# Revit family: Ventüer_VentilationLouvres_VL-77EX
name_source: partatom
category: Generic Models
units: mm (PartAtom-declared; Revit-internal decimal feet)

## family parameters
Always vertical = No
Can host rebar = No
Cut with Voids When Loaded = Yes
Part Type = Normal
Room Calculation Point = No
Round Connector Dimension = Use Diameter
Shared = No
Work Plane-Based = Yes

## types (3) — shared parameters
Aerodynamic Performance = Air Inlet: 0.244, Class 3. Air Extract: 0.255, Class 3
Ancillaries = Bird Mesh, Insect Mesh, Solid Blanking, Electric Actuators, Manual Lever Handles, Perimeter Mounting Angle
Blade Centres = 77 mm  [stored 0.252625 ft]
Blade Material = Ventüer Aluminium
Default Elevation = 1219 mm
Description = Maximum Airflow for Exhaust
Exact Neck Height = 594 mm  [stored 1.94882 ft]
Exact Neck Height Check = 594 mm  [stored 1.94882 ft]
Exact Neck Width = 594 mm  [stored 1.94882 ft]
Exact Neck Width Check = 594 mm  [stored 1.94882 ft]
Frame Material = Ventüer Aluminium
Frame Set Count = 1
Frame Set Count Check = 2
Frame Set Transition Count = 1
Frame Set Transition Count Check = 2
Manufacturer = Ventüer
Max Flow = 5000.0 L/s
Min Flow = 100.0 L/s
Model = VL-77EX
Multiple Frame Set = No
Multiple Transition = No
Noise Level NC Max = 0.00 NC
Noise Level NC Min = 0.00 NC
Nominal Height = 600 mm
Nominal Width = 600 mm
Nominated Air Flow = 100.0 L/s
Nominated Pessure Drop = 21.0 Pa
Rain Defence Performance = Class B - up to 0.5m/s suction velocity. Class C - up to 1.5m/s suction velocity. Class D - up to 3.5m/s suction velocity
SHS = No
Single Frame Set = Yes
Single Transition = No
Specified Air Flow = 0.0 L/s
Specified Pressure Drop = 21.0 Pa
Static Pressure Max = 60.0 Pa
Static Pressure Min = 10.0 Pa
Tee = Yes
URL = https://www.ventuer.co
Ventüer Product Range = Ventilation Louvres

## per-type parameters (varying)
| type | Base Width | Blade And Frame Gap | Blade Count | Blade Cut Offset | Blade Horizontal Offset | Channel | Connector Height | Connector Width | Depth | Flanged | Frame Set Width | Glazed | Keynote | Overall Opening Height | Overall Opening Width | Profile Width | Screen Symbol Distance | Siffener Length | Single Frame Set Width | Top Blade | Top Blade Corrector | Top Blade Height |
| VL-77EX_CF | 3 mm  [stored 0.00984252 ft] | 32 mm  [stored 0.104987 ft] | 7 | 539 mm  [stored 1.76837 ft] | 6 mm  [stored 0.019685 ft] | Yes | 588 mm | 588 mm | 100 mm  [stored 0.328084 ft] | No | 588 mm | No | VL-77EX_FF | 588 mm | 588 mm | 3 mm  [stored 0.00984252 ft] | 4 mm  [stored 0.0131234 ft] | 588 mm | 294 mm | No | 0 mm  [stored 0 ft] | 17 mm |
| VL-77EX_GF | 26 mm | 10 mm  [stored 0.0328084 ft] | 6 | 462 mm  [stored 1.51575 ft] | 8 mm  [stored 0.0262467 ft] | No | 532 mm | 532 mm | 105 mm  [stored 0.344488 ft] | No | 521 mm | Yes | VL-77EX_GF | 532 mm | 532 mm | 37 mm | 6 mm  [stored 0.019685 ft] | 542 mm  [stored 1.77822 ft] | 261 mm | Yes | 11 mm | 70 mm |
| VL-77EX_FF | 52 mm | 10 mm  [stored 0.0328084 ft] | 6 | 462 mm  [stored 1.51575 ft] | 6 mm  [stored 0.019685 ft] | No | 490 mm  [stored 1.60761 ft] | 490 mm  [stored 1.60761 ft] | 101 mm | Yes | 490 mm  [stored 1.60761 ft] | No | VL-77EX_FF | 490 mm  [stored 1.60761 ft] | 490 mm  [stored 1.60761 ft] | 52 mm | 4 mm  [stored 0.0131234 ft] | 490 mm  [stored 1.60761 ft] | 245 mm  [stored 0.803806 ft] | No | 0 mm  [stored 0 ft] | 18 mm  [stored 0.0590551 ft] |

note: [stored X ft] marks values corroborated as IEEE doubles in the binary element streams (Revit-internal decimal feet)

## geometry (parser evidence)
native form markers: Sweep x47
no freeform markers — native parametric forms only
